# Revit family: 63-SANITARIO AQUAJET COLOR BLANCO
name_source: partatom
category: Aparatos sanitarios
revit_build: Autodesk Revit 2018 (Build: 20170223_1515(x64)
units: mm (PartAtom-declared; Revit-internal decimal feet)

## family parameters
Anfitrión = Muro
Compartido = No
Corte con vacíos al cargar = No
Cota de conector redondo = Diámetro de uso
Número OmniClass = 23.45.55.00
Punto de cálculo de habitación = No
Siempre vertical = Sí
Tipo de pieza = Normal
Título OmniClass = Sanitary Faucets, Wastes

## types (1)
- Tipo 1
    Acabado = Brillante
    Alto Nominal = 768 mm  [stored 2.51969 ft]
    Ancho Nominal = 480 mm  [stored 1.5748 ft]
    Característica = Cómoda taza alongada, funcional diseño contemporáneo, válvula antisifón sifón 100% esmaltado t mayor diámetro optimiza el funcionamiento y mejora la limpieza, sistema de desacarga por gravedad, evacuación de sólidos 400 gr.
    Color = Blanco
    Consumo de Agua = 6 LPF.
    Cumplimiento de Norma = Cumple requerimientos ADA para accesibilidad, norma NTC 920-1
    Código de montaje = D2030
    Descripción = Sanitary Waste
    Descripción de la garantía = Porcelana sanitaria garantía de por vida, garantía de 5 años para grifería
    Diámetro de conexión de entrada = 12,7 mm / 1/2"
    Diámetro de conexión sanitaria = 101.6 mm / 4"
    Duración Garantía Partes = Integral de por vida
    Duración Garantía Unidad = Años
    Fabricante = www.corona.com.co
    Forma = Rectangular
    Imagen de tipo = <Ninguno>
    Informacion del producto = https://corona.co
    Longitud Nominal = 744 mm  [stored 2.44094 ft]
    Material = Ceramica_Corona_Blanco
    Material Secundario = Plastico_Corona_Blanco
    Nombre = Aquajet
    Numero de Modelo = O26401001
    Presión máxima = 125 PSI
    Presión mínima = 15 PSI
    Requerimientos de Accesibilidad = Manual
    Responsable Garantia Partes = www.corona.com.co
    Tamaño = 744 x 480 x 768
    Tipo de Activo = Fijo
    Tráfico = Institucional

note: [stored X ft] marks values corroborated as IEEE doubles in the binary element streams (Revit-internal decimal feet)
